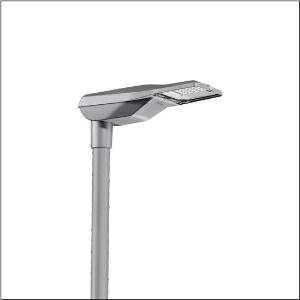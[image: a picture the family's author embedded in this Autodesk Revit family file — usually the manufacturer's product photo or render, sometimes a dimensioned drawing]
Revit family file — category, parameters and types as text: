
# Revit family: streetlight_sl_21_micro___st1_0a_5xe5d23a08cb_0faa
name_source: partatom
category: Lighting Fixtures
units: mm (PartAtom-declared; Revit-internal decimal feet)

## family parameters
Cut with Voids When Loaded = No
Host = Face
Light Source = No
Part Type = Normal
Room Calculation Point = No
Round Connector Dimension = Use Diameter
Shared = No

## types (1)
- --- (1 x LED, 1900 lm, 15.8 W, 2200K)
    Apparent Load = 16 VA
    CIE Flux Codes = 37 72 97 100 100
    Color Rendering = 70
    Color Temperature = 2200K
    Default Elevation = 1800 mm
    Description = Streetlight SL 21 micro, mast luminaire, primary light control with lens, of PMMA, primary optical cover: cover, of toughened safety glass, transparent, light distribution: ST1.0a, light emission: direct distribution, primary light characteristic: asymmetric, installation type: side-entry, post-top, LED, 3G 1.5mm², High Power LED, rated luminous flux: 1.900lm, luminous efficacy: 120lm/W, light colour: 722, colour temperature: 2200K, control: flexible luminous flux parameterisation, time-dependent luminous flux control, constant luminous flux control, overheat protection, mains connection: 230..240V, AC, 50/60Hz, connection cable pre-assembled, cable length: 5,5m, wiring characteristics: H07RN-F, start of lifetime: 16W, end of service life: 16W, reduction: 8W, luminaire housing, of diecast aluminium, powder-coated, Siteco® metallic grey (DB 702S), corrosivity category C5 mid according to DIN EN ISO 12944, please order mast flange separately, inclination adjustable: 0°, 5°, 10°, 15°, sealing non-destructively replaceable, multi-level sealing system, length: 528mm, width: 235mm, height: 110mm, mast flange for spigot size: 42mm (side-entry): 5XC10008XM4, 60/48mm (side-entry/post-top): 5XC10108XM2, 76/60mm (side-entry/post-top): 5XC10108XM1, protection rating (complete): IP66, insulation class (complete): insulation class II (safety insulation), certification: CE, ENEC, ENEC+, VDE, impact resistance: IK09, permissible operating ambient temperature for outdoor applications: -40..+50°C, standard-compliant lighting for roads and squares, packaging unit: 1 piece

Light Distribution: ST1.0a
    Height = 110 mm
    Lamp = 1 x LED
    Lamp Light Flux = 1900 lm
    Lamp Power = 15.8 W
    Lamp count = 1
    Length = 528 mm
    Luminous efficacy = 120 lm/W
    Manufacturer = Siteco
    ModVariant = No
    Model = 5XE5D23A08CB
    Number of Poles = 1
    OnlyDefault = Yes
    Power Factor = 1
    Product Name = Streetlight SL 21 micro | ST1.0a
    Product group = mast luminaire | pylon top
    ProductGroupID = 6100
    Protection Class = Protection class II
    Protection Degree = IP 66
    RLX_Detail_Level = 1
    RLX_Emergency_Light_Flux = 0 lm
    RLX_Emergency_Type = 0
    RLX_Emergency_Type_DB = No
    RlxData = <blob elided: 98033 chars, md5=0d87a713>
    Socket = socket
    Standby Power = 0 W
    System Light Flux = 1900 lm
    System Power = 16 W
    Type Comments = factory setting: luminous flux: 100 % | Output Level: 100 % | 300 mA
    Type Image = l_1006881.jpg
    URL = http://relux.com
    VarID = @adj_105849
    Voltage = 0 V
    Weight = 0.00 kg
    Width = 235 mm

## geometry (parser evidence)
native form markers: Blend x4, Sweep x10
no freeform markers — native parametric forms only
